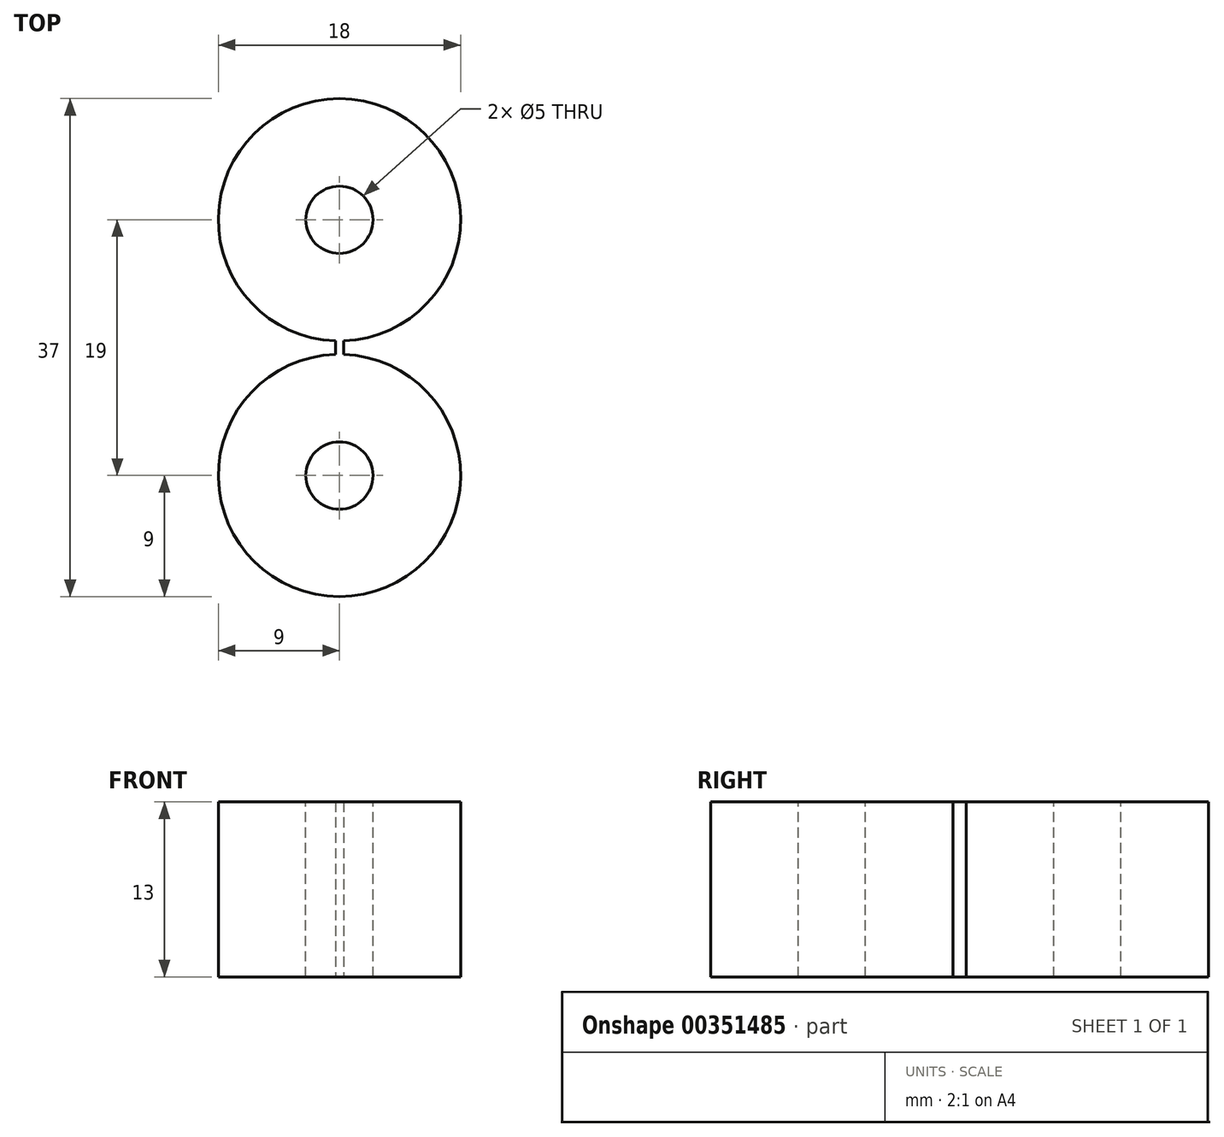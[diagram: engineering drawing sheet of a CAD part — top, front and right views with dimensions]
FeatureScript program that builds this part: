
annotation { "Feature Type Name" : "Feature", "Feature Type Description" : "" }
export const myFeature = defineFeature(function(context is Context, id is Id, definition is map)
    precondition{}
    {
        {
            var Q0;
            Q0=qCreatedBy(makeId("Top.planeOp"),FACE);
            var sketch = newSketch(context, id + "F0", { "sketchPlane" : qUnion([Q0])});
            skCircle(sketch, "E0", {"center": v(0, 0) * mm, "radius": 9 * mm});
            skSolve(sketch);
        }
        {
            var Q0;
            Q0 = qSketchRegion(id + "F0", true);
            extrude(context, id + "F1", {"entities" : qUnion([Q0]), "depth" : 13 * mm});
        }
        {
            var Q0;
            Q0=makeQuery(id+"F1.opExtrude","CAP_FACE",FACE,{"disambiguationData":[OSD([sQuery(id+"F0.wireOp",EDGE,"E0")])],"isStart":false});
            var sketch = newSketch(context, id + "F2", { "sketchPlane" : qUnion([Q0])});
            skCircle(sketch, "E1", {"center": v(0, 0) * mm, "radius": 2.5 * mm});
            skSolve(sketch);
        }
        {
            var Q0;
            Q0=makeQuery(id+"F2.imprint","IMPRINT",FACE,{"disambiguationData":[TD([[makeQuery(id+"F2.imprint","IMPRINT",EDGE,{"derivedFrom":sQuery(id+"F2.wireOp",EDGE,"E1")}),1.0]])]});
            extrude(context, id + "F3", {"entities" : qUnion([Q0]), "operationType" : NewBodyOperationType.REMOVE, "endBound" : BoundingType.THROUGH_ALL, "oppositeDirection" : true, "depth" : 25 * mm});
        }
        {
            var Q0;
            Q0=qCreatedBy(makeId("Front.planeOp"),FACE);
            cPlane(context, id + "F4", {"entities" : qUnion([Q0]), "cplaneType" : CPlaneType.OFFSET, "offset" : 9.5 * mm, "width" : 150 * mm, "height" : 150 * mm});
        }
        {
            var Q0;
            Q0=qCreatedBy(id+"F4.planeOp",FACE);
            var sketch = newSketch(context, id + "F5", { "sketchPlane" : qUnion([Q0])});
            skLineSegment(sketch, "E2.0", {"start": v(-9, 13) * mm, "end": v(9, 13) * mm, "construction": true});
            skLineSegment(sketch, "E3.0", {"start": v(-9, 0) * mm, "end": v(9, 0) * mm, "construction": true});
            skLineSegment(sketch, "E4", {"start": v(0, 0) * mm, "end": v(0, 13) * mm, "construction": true});
            skLineSegment(sketch, "E5.bottom", {"start": v(0.3, 0) * mm, "end": v(-0.3, 0) * mm});
            skLineSegment(sketch, "E5.top", {"start": v(0.3, 13) * mm, "end": v(-0.3, 13) * mm});
            skLineSegment(sketch, "E5.left", {"start": v(0.3, 0) * mm, "end": v(0.3, 13) * mm});
            skLineSegment(sketch, "E5.right", {"start": v(-0.3, 0) * mm, "end": v(-0.3, 13) * mm});
            skPoint(sketch, "E5.middle", {"position": v(0, 6.5) * mm});
            skSolve(sketch);
        }
        {
            var Q0;
            Q0=makeQuery(id+"F1.opExtrude","SWEPT_BODY",BODY,{"disambiguationData":[OSD([sQuery(id+"F0.wireOp",EDGE,"E0")])]});
            var Q1;
            Q1=makeQuery(id+"F5.imprint","IMPRINT",FACE,{"disambiguationData":[TD([[makeQuery(id+"F5.imprint","IMPRINT",EDGE,{"derivedFrom":sQuery(id+"F5.wireOp",EDGE,"E5.bottom")}),-1.0]])]});
            mirror(context, id + "F6", {"entities" : qUnion([Q0]), "mirrorPlane" : qUnion([Q1])});
        }
        {
            var Q0;
            Q0 = qSketchRegion(id + "F5", true);
            var Q1;
            Q1=makeQuery(id+"F6.opPattern","COPY",FACE,{"derivedFrom":makeQuery(id+"F1.opExtrude","SWEPT_FACE",FACE,{"disambiguationData":[OSD([sQuery(id+"F0.wireOp",EDGE,"E0")])]}),"instanceName":"1"});
            var Q2;
            Q2=makeQuery(id+"F1.opExtrude","SWEPT_FACE",FACE,{"disambiguationData":[OSD([sQuery(id+"F0.wireOp",EDGE,"E0")])]});
            extrude(context, id + "F7", {"entities" : qUnion([Q0]), "operationType" : NewBodyOperationType.ADD, "endBound" : BoundingType.UP_TO_SURFACE, "endBoundEntityFace" : qUnion([Q1]), "depth" : 25 * mm, "hasSecondDirection" : true, "secondDirectionBound" : SecondDirectionBoundingType.UP_TO_SURFACE, "secondDirectionOppositeDirection" : true, "secondDirectionBoundEntityFace" : qUnion([Q2]), "secondDirectionDepth" : 25 * mm});
        }
    });
